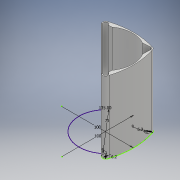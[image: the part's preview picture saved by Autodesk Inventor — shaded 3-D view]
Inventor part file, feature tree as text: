
AUTODESK INVENTOR PART (.ipt)
format: ipt  version: 2017 (Build 210142000, 142)  size: 127,488 bytes
history: native  units: mm
features: extrude x1, sketch x1
ambient origin geometry x8: Origin, YZ Plane, XZ Plane, XY Plane, X Axis, Y Axis, Z Axis, Center Point
bodies: Solid1 (feature_tree)
feature tree (2):
  extrude  "Extrusion1"  Depth=100.0mm
  sketch  "Sketch1"  dims[d0=6.2mm d1=6.2mm d6=9.0mm d7=9.0mm d8=135.0deg d9=75.0mm d11=100.0mm d12=100.0mm d13=100.0mm d14=0.0mm]
